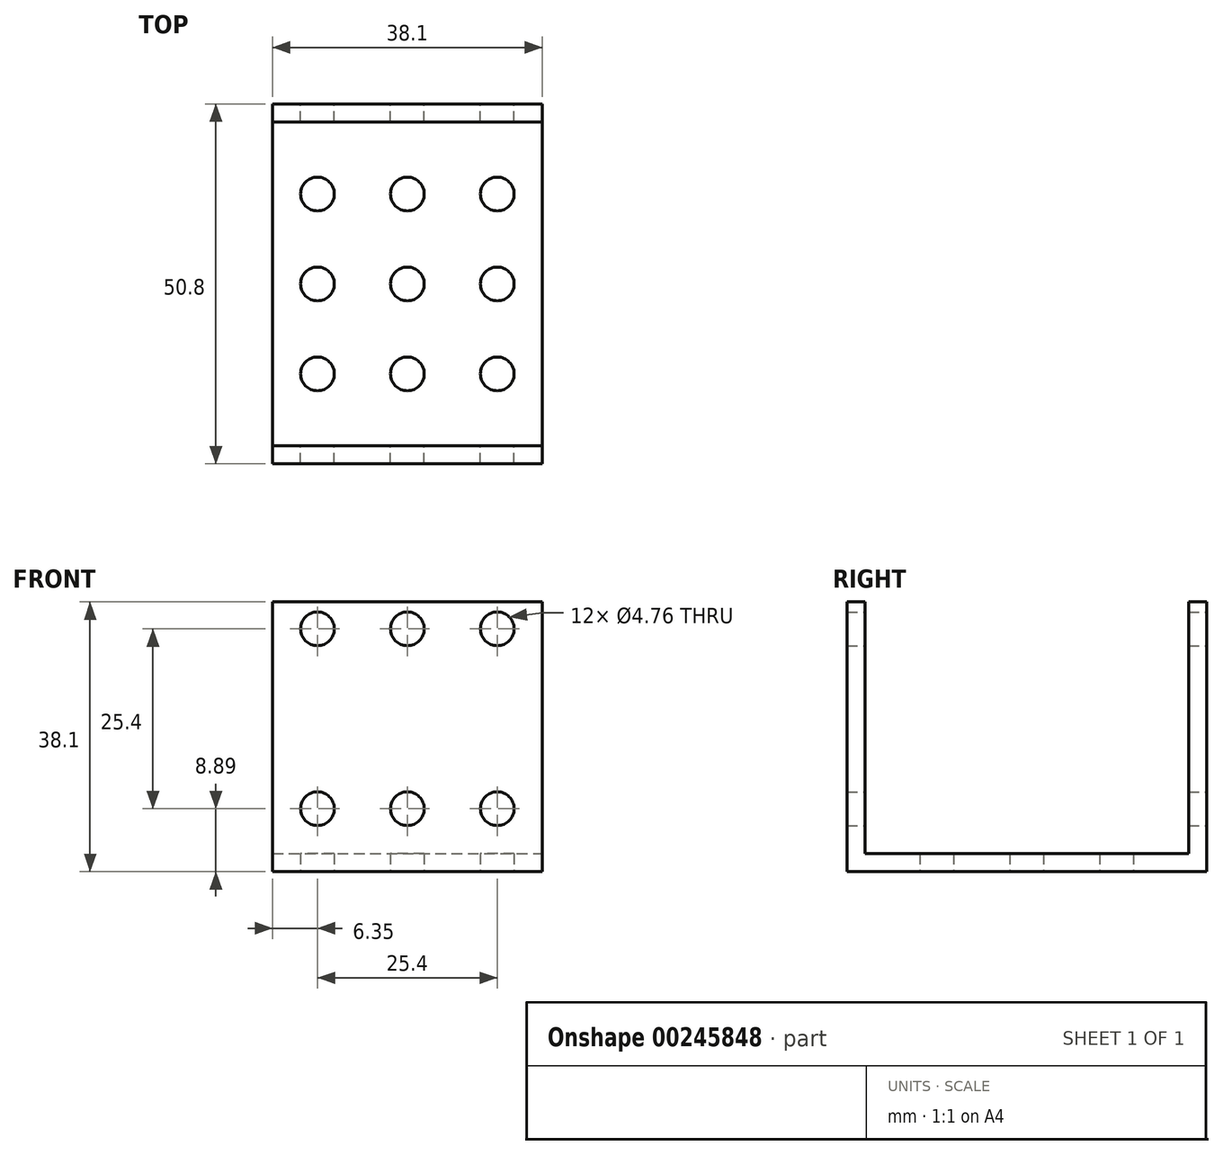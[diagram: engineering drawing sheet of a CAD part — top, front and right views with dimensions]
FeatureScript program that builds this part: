
annotation { "Feature Type Name" : "Feature", "Feature Type Description" : "" }
export const myFeature = defineFeature(function(context is Context, id is Id, definition is map)
    precondition{}
    {
        {
            var Q0;
            Q0=qCreatedBy(makeId("Top.planeOp"),FACE);
            var sketch = newSketch(context, id + "F0", { "sketchPlane" : qUnion([Q0])});
            skLineSegment(sketch, "E0.bottom", {"start": v(-19.05, 22.86) * mm, "end": v(19.05, 22.86) * mm});
            skLineSegment(sketch, "E0.top", {"start": v(-19.05, -22.86) * mm, "end": v(19.05, -22.86) * mm});
            skLineSegment(sketch, "E0.left", {"start": v(-19.05, 22.86) * mm, "end": v(-19.05, -22.86) * mm});
            skLineSegment(sketch, "E0.right", {"start": v(19.05, 22.86) * mm, "end": v(19.05, -22.86) * mm});
            skPoint(sketch, "E0.middle", {"position": v(0, 0) * mm});
            skLineSegment(sketch, "E1.top", {"start": v(-19.05, 25.4) * mm, "end": v(19.05, 25.4) * mm});
            skLineSegment(sketch, "E1.left", {"start": v(-19.05, 22.86) * mm, "end": v(-19.05, 25.4) * mm});
            skLineSegment(sketch, "E1.right", {"start": v(19.05, 22.86) * mm, "end": v(19.05, 25.4) * mm});
            skLineSegment(sketch, "E2.top", {"start": v(-19.05, -25.4) * mm, "end": v(19.05, -25.4) * mm});
            skLineSegment(sketch, "E2.left", {"start": v(-19.05, -22.86) * mm, "end": v(-19.05, -25.4) * mm});
            skLineSegment(sketch, "E2.right", {"start": v(19.05, -22.86) * mm, "end": v(19.05, -25.4) * mm});
            skCircle(sketch, "E3", {"center": v(-12.7, -12.7) * mm, "radius": 2.38 * mm});
            skCircle(sketch, "E4.0.1.0", {"center": v(-12.7, 0) * mm, "radius": 2.38 * mm});
            skCircle(sketch, "E4.0.2.0", {"center": v(-12.7, 12.7) * mm, "radius": 2.38 * mm});
            skCircle(sketch, "E4.1.0.0", {"center": v(0, -12.7) * mm, "radius": 2.38 * mm});
            skCircle(sketch, "E4.1.1.0", {"center": v(0, 0) * mm, "radius": 2.38 * mm});
            skCircle(sketch, "E4.1.2.0", {"center": v(0, 12.7) * mm, "radius": 2.38 * mm});
            skCircle(sketch, "E4.2.0.0", {"center": v(12.7, -12.7) * mm, "radius": 2.38 * mm});
            skCircle(sketch, "E4.2.1.0", {"center": v(12.7, 0) * mm, "radius": 2.38 * mm});
            skCircle(sketch, "E4.2.2.0", {"center": v(12.7, 12.7) * mm, "radius": 2.38 * mm});
            skLineSegment(sketch, "E4.direction1", {"start": v(-12.7, -12.7) * mm, "end": v(0, -12.7) * mm, "construction": true});
            skLineSegment(sketch, "E4.direction2", {"start": v(-12.7, -12.7) * mm, "end": v(-12.7, 0) * mm, "construction": true});
            skSolve(sketch);
        }
        {
            var Q0;
            Q0=makeQuery(id+"F0.imprint","IMPRINT",FACE,{"disambiguationData":[TD([[makeQuery(id+"F0.imprint","IMPRINT",EDGE,{"derivedFrom":sQuery(id+"F0.wireOp",EDGE,"E0.left")}),1.0]])]});
            extrude(context, id + "F1", {"entities" : qUnion([Q0]), "depth" : 2.54 * mm});
        }
        {
            var Q0;
            Q0=makeQuery(id+"F0.imprint","IMPRINT",FACE,{"disambiguationData":[TD([[makeQuery(id+"F0.imprint","IMPRINT",EDGE,{"derivedFrom":sQuery(id+"F0.wireOp",EDGE,"E0.bottom")}),1.0]])]});
            var Q1;
            Q1=makeQuery(id+"F0.imprint","IMPRINT",FACE,{"disambiguationData":[TD([[makeQuery(id+"F0.imprint","IMPRINT",EDGE,{"derivedFrom":sQuery(id+"F0.wireOp",EDGE,"E0.top")}),-1.0]])]});
            extrude(context, id + "F2", {"entities" : qUnion([Q0, Q1]), "operationType" : NewBodyOperationType.ADD, "depth" : 38.1 * mm});
        }
        {
            var Q0;
            Q0=makeQuery(id+"F2.opExtrude","SWEPT_FACE",FACE,{"disambiguationData":[OSD([sQuery(id+"F0.wireOp",EDGE,"E1.top")])]});
            var sketch = newSketch(context, id + "F3", { "sketchPlane" : qUnion([Q0])});
            skLineSegment(sketch, "E5", {"start": v(0, 38.1) * mm, "end": v(0, 0) * mm, "construction": true});
            skLineSegment(sketch, "E6", {"start": v(-6.35, 38.1) * mm, "end": v(-6.35, 0) * mm, "construction": true});
            skLineSegment(sketch, "E7", {"start": v(6.35, 38.1) * mm, "end": v(6.35, 0) * mm, "construction": true});
            skLineSegment(sketch, "E8", {"start": v(12.7, 38.1) * mm, "end": v(12.7, 0) * mm, "construction": true});
            skLineSegment(sketch, "E9", {"start": v(-12.7, 38.1) * mm, "end": v(-12.7, 0) * mm, "construction": true});
            skCircle(sketch, "E10", {"center": v(-12.7, 34.3) * mm, "radius": 2.38 * mm});
            skCircle(sketch, "E11", {"center": v(0, 34.3) * mm, "radius": 2.38 * mm});
            skCircle(sketch, "E12", {"center": v(12.7, 34.3) * mm, "radius": 2.38 * mm});
            skCircle(sketch, "E13", {"center": v(-12.7, 8.9) * mm, "radius": 2.38 * mm});
            skCircle(sketch, "E14", {"center": v(0, 8.9) * mm, "radius": 2.38 * mm});
            skCircle(sketch, "E15", {"center": v(12.7, 8.9) * mm, "radius": 2.38 * mm});
            skSolve(sketch);
        }
        {
            var Q0;
            Q0=makeQuery(id+"F3.imprint","IMPRINT",FACE,{"disambiguationData":[TD([[makeQuery(id+"F3.imprint","IMPRINT",EDGE,{"derivedFrom":sQuery(id+"F3.wireOp",EDGE,"E10")}),1.0]])]});
            var Q1;
            Q1=makeQuery(id+"F3.imprint","IMPRINT",FACE,{"disambiguationData":[TD([[makeQuery(id+"F3.imprint","IMPRINT",EDGE,{"derivedFrom":sQuery(id+"F3.wireOp",EDGE,"E11")}),1.0]])]});
            var Q2;
            Q2=makeQuery(id+"F3.imprint","IMPRINT",FACE,{"disambiguationData":[TD([[makeQuery(id+"F3.imprint","IMPRINT",EDGE,{"derivedFrom":sQuery(id+"F3.wireOp",EDGE,"E12")}),1.0]])]});
            var Q3;
            Q3=makeQuery(id+"F3.imprint","IMPRINT",FACE,{"disambiguationData":[TD([[makeQuery(id+"F3.imprint","IMPRINT",EDGE,{"derivedFrom":sQuery(id+"F3.wireOp",EDGE,"E15")}),1.0]])]});
            var Q4;
            Q4=makeQuery(id+"F3.imprint","IMPRINT",FACE,{"disambiguationData":[TD([[makeQuery(id+"F3.imprint","IMPRINT",EDGE,{"derivedFrom":sQuery(id+"F3.wireOp",EDGE,"E14")}),1.0]])]});
            var Q5;
            Q5=makeQuery(id+"F3.imprint","IMPRINT",FACE,{"disambiguationData":[TD([[makeQuery(id+"F3.imprint","IMPRINT",EDGE,{"derivedFrom":sQuery(id+"F3.wireOp",EDGE,"E13")}),1.0]])]});
            extrude(context, id + "F4", {"entities" : qUnion([Q0, Q1, Q2, Q3, Q4, Q5]), "operationType" : NewBodyOperationType.REMOVE, "endBound" : BoundingType.THROUGH_ALL, "oppositeDirection" : true, "depth" : 25.4 * mm});
        }
    });
